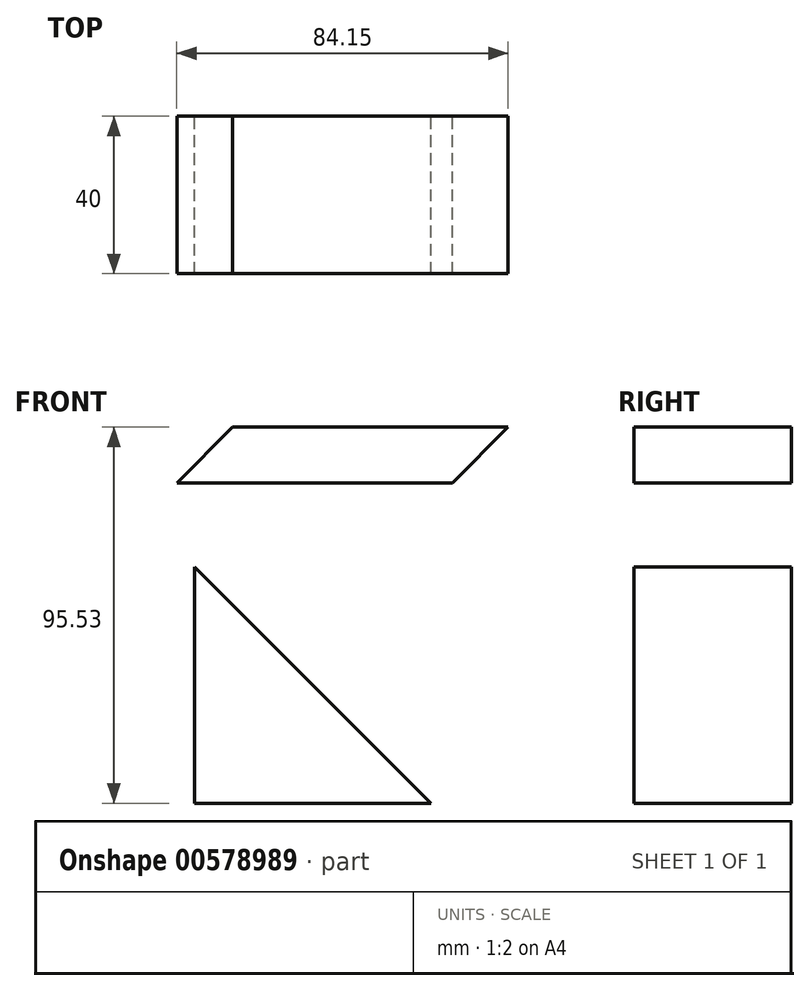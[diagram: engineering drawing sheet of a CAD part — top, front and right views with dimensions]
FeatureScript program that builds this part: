
annotation { "Feature Type Name" : "Feature", "Feature Type Description" : "" }
export const myFeature = defineFeature(function(context is Context, id is Id, definition is map)
    precondition{}
    {
        {
            var Q0;
            Q0=qCreatedBy(makeId("Front.planeOp"),FACE);
            var sketch = newSketch(context, id + "F0", { "sketchPlane" : qUnion([Q0])});
            skLineSegment(sketch, "E0", {"start": v(-64.32, 16.43) * mm, "end": v(-50.17, 30.57) * mm});
            skLineSegment(sketch, "E1", {"start": v(-50.17, 30.57) * mm, "end": v(19.83, 30.57) * mm});
            skLineSegment(sketch, "E2", {"start": v(19.83, 30.57) * mm, "end": v(5.68, 16.43) * mm});
            skLineSegment(sketch, "E3", {"start": v(5.68, 16.43) * mm, "end": v(-64.32, 16.43) * mm});
            skSolve(sketch);
        }
        {
            var Q0;
            Q0=qCreatedBy(makeId("Front.planeOp"),FACE);
            var sketch = newSketch(context, id + "F1", { "sketchPlane" : qUnion([Q0])});
            skLineSegment(sketch, "E4", {"start": v(-59.76, -4.96) * mm, "end": v(-59.76, -64.96) * mm});
            skLineSegment(sketch, "E5", {"start": v(-59.76, -64.96) * mm, "end": v(0.24, -64.96) * mm});
            skLineSegment(sketch, "E6", {"start": v(0.24, -64.96) * mm, "end": v(-59.76, -4.96) * mm});
            skSolve(sketch);
        }
        {
            var Q0;
            Q0 = qSketchRegion(id + "F1", true);
            var Q1;
            Q1 = qSketchRegion(id + "F0", true);
            extrude(context, id + "F2", {"entities" : qUnion([Q0, Q1]), "depth" : 40 * mm, "offsetDistance" : 25 * mm});
        }
    });
